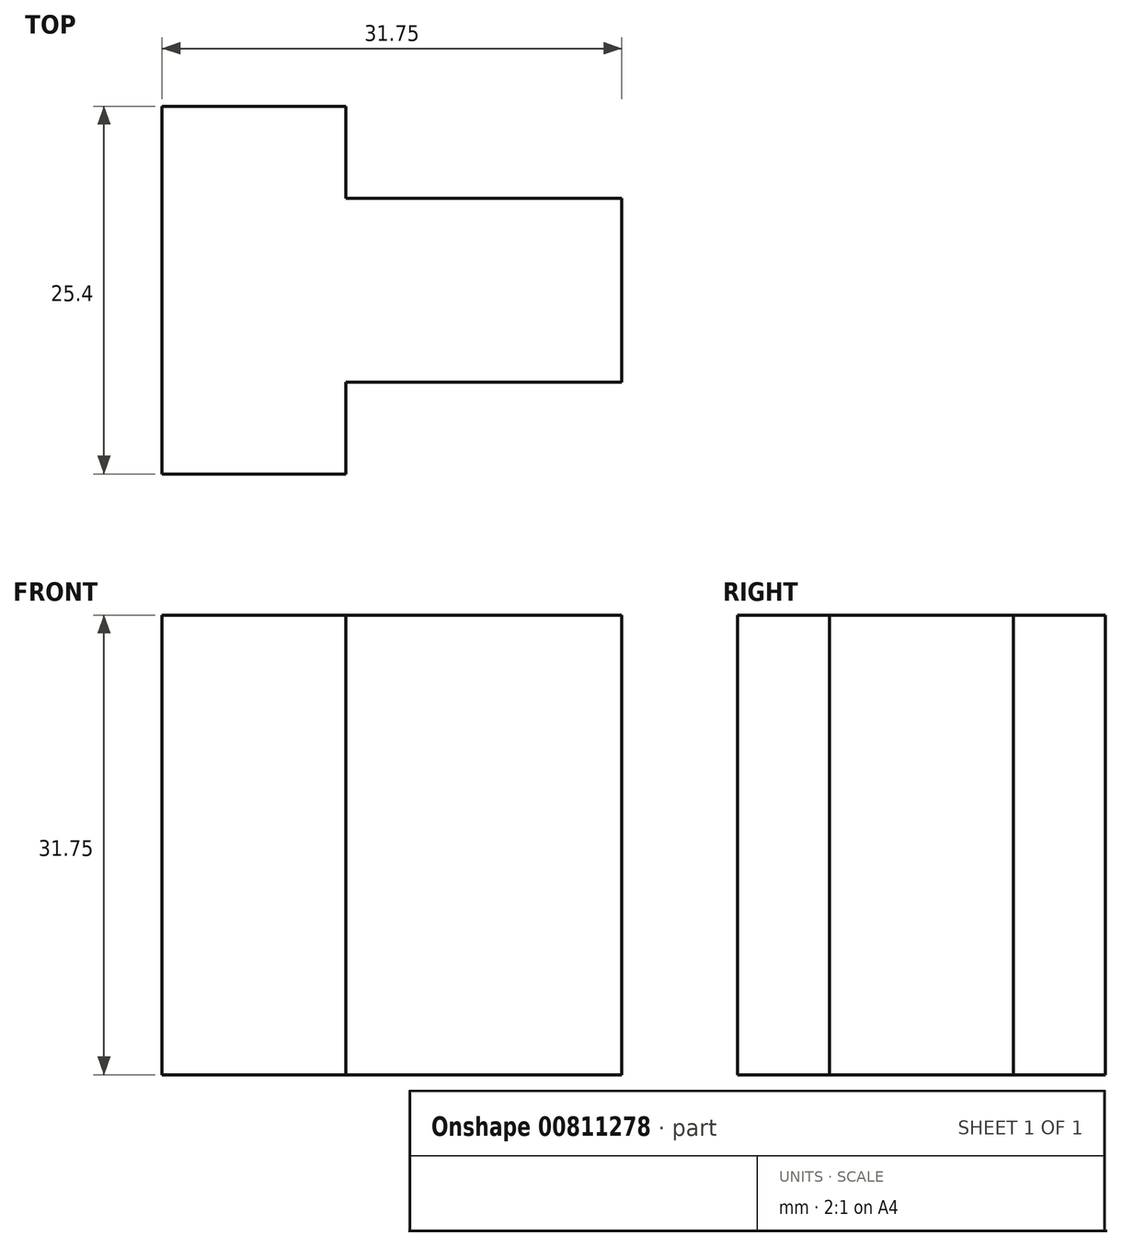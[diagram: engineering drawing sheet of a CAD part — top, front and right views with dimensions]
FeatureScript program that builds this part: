
annotation { "Feature Type Name" : "Feature", "Feature Type Description" : "" }
export const myFeature = defineFeature(function(context is Context, id is Id, definition is map)
    precondition{}
    {
        {
            var Q0;
            Q0=qCreatedBy(makeId("Top.planeOp"),FACE);
            var sketch = newSketch(context, id + "F0", { "sketchPlane" : qUnion([Q0])});
            skLineSegment(sketch, "E0", {"start": v(0, 25.4) * mm, "end": v(0, 0) * mm});
            skLineSegment(sketch, "E1", {"start": v(12.7, 0) * mm, "end": v(0, 0) * mm});
            skLineSegment(sketch, "E2", {"start": v(0, 25.4) * mm, "end": v(12.7, 25.4) * mm});
            skLineSegment(sketch, "E3", {"start": v(12.7, 19.05) * mm, "end": v(12.7, 25.4) * mm});
            skLineSegment(sketch, "E4", {"start": v(12.7, 6.35) * mm, "end": v(12.7, 0) * mm});
            skLineSegment(sketch, "E5", {"start": v(12.7, 19.05) * mm, "end": v(31.75, 19.05) * mm});
            skLineSegment(sketch, "E6", {"start": v(12.7, 6.35) * mm, "end": v(31.75, 6.35) * mm});
            skLineSegment(sketch, "E7", {"start": v(31.75, 19.05) * mm, "end": v(31.75, 6.35) * mm});
            skSolve(sketch);
        }
        {
            var Q0;
            Q0=makeQuery(id+"F0.imprint","IMPRINT",FACE,{"disambiguationData":[TD([[makeQuery(id+"F0.imprint","IMPRINT",EDGE,{"derivedFrom":sQuery(id+"F0.wireOp",EDGE,"E0")}),1.0]])]});
            extrude(context, id + "F1", {"entities" : qUnion([Q0]), "depth" : 31.75 * mm, "offsetDistance" : 25.4 * mm});
        }
    });
